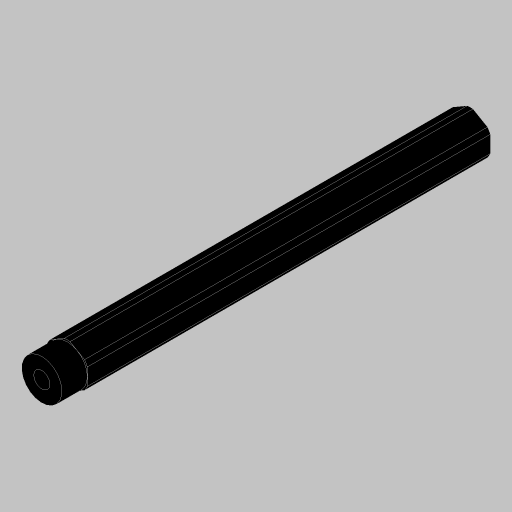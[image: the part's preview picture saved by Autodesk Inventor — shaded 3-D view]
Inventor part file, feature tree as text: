
AUTODESK INVENTOR PART (.ipt)
format: ipt  version: 2023.5 (Build 275446000, 446)  size: 141,312 bytes
history: native  units: in
note: dims shown in document units (in); Inventor stores cm internally (conversion verified against a paired STEP export)
features: extrude x3, projected_geometry x3, hole x1, sketch x1
ambient origin geometry x8: Origin, YZ Plane, XZ Plane, XY Plane, X Axis, Y Axis, Z Axis, Center Point
bodies: Solid1 (feature_tree)
feature tree (8):
  extrude  "Extrusion1"  Depth=0.315in
  hole  "Hole1"  [1 undecoded]
  extrude  "Extrusion3"  Depth=0.5in
  extrude  "Extrusion4"  Depth=0.315in TaperAngle=0.0deg
  sketch  "Sketch5"  dims[d2=0.0in d9=0.625in d10=0.385in d11=0.25in d12=0.5635in d13=1.0in d14=0.8108in d16=0.7in d17=0.0in d18=0.0in d19=0.5in d20=0.315in d21=0.0in]
  projected_geometry  "Project Cut Edges1"
  projected_geometry  "Project Cut Edges2"
  projected_geometry  "Project Cut Edges3"
note: 1 required parameter value undecoded (feature->parameter linkage not recoverable at this tier; creation-order binding heuristic only, values carry confidence <= 0.55)
